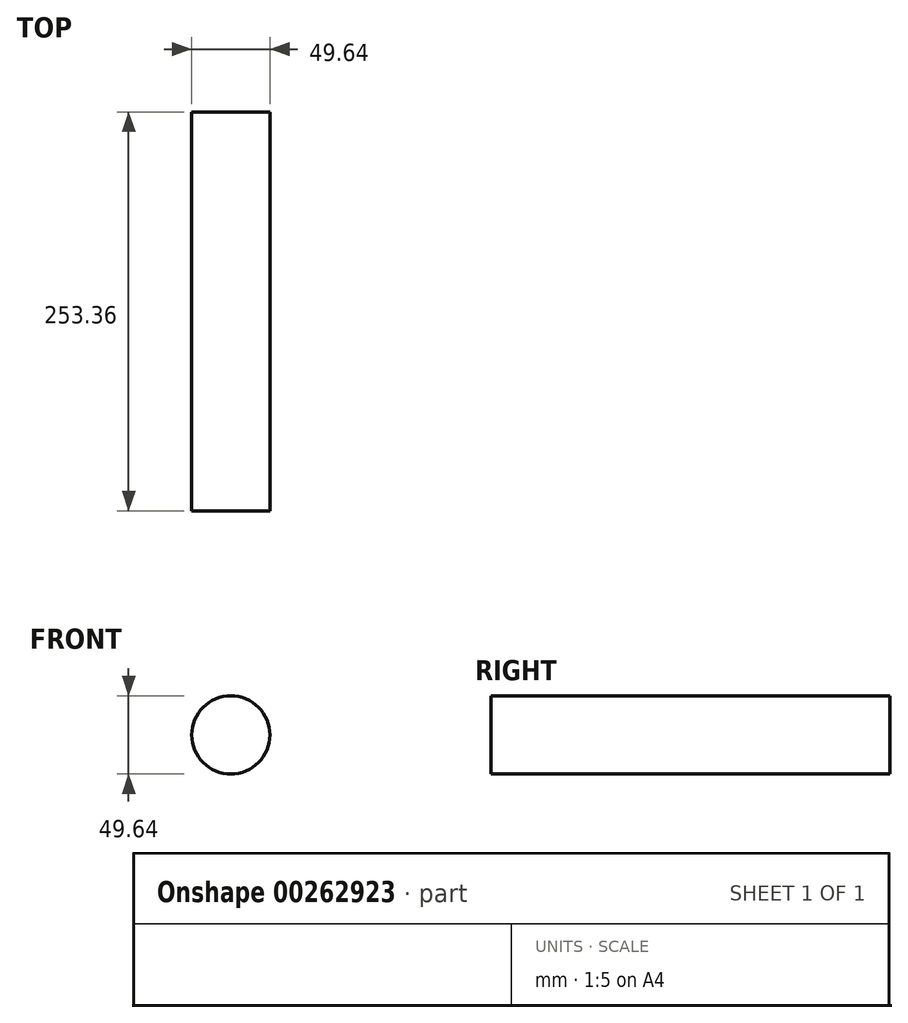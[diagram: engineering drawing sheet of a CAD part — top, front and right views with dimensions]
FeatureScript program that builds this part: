
annotation { "Feature Type Name" : "Feature", "Feature Type Description" : "" }
export const myFeature = defineFeature(function(context is Context, id is Id, definition is map)
    precondition{}
    {
        {
            var Q0;
            Q0=qCreatedBy(makeId("Front.planeOp"),FACE);
            var sketch = newSketch(context, id + "F0", { "sketchPlane" : qUnion([Q0])});
            skCircle(sketch, "E0", {"center": v(0, 0) * mm, "radius": 24.82 * mm});
            skSolve(sketch);
        }
        {
            var Q0;
            Q0=makeQuery(id+"F0.imprint","IMPRINT",FACE,{"disambiguationData":[TD([[makeQuery(id+"F0.imprint","IMPRINT",EDGE,{"derivedFrom":sQuery(id+"F0.wireOp",EDGE,"E0")}),1.0]])]});
            var Q1;
            Q1 = qSketchRegion(id + "F0", true);
            extrude(context, id + "F1", {"entities" : qUnion([Q0, Q1]), "depth" : 253.36 * mm});
        }
    });
